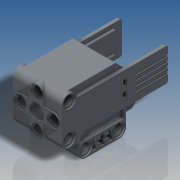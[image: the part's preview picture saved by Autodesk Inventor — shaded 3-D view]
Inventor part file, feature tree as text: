
AUTODESK INVENTOR PART (.ipt)
format: ipt  version: 2016 SP2 (Build 200236200, 236)  size: 1,027,584 bytes
history: native  units: in
note: dims shown in document units (in); Inventor stores cm internally (conversion verified against a paired STEP export)
features: extrude x12, sketch x7, plane x2, mirror x2, revolve x1, fillet x1
ambient origin geometry x8: Origin, YZ Plane, XZ Plane, XY Plane, X Axis, Y Axis, Z Axis, Center Point
bodies: Solid1 (feature_tree)
feature tree (25):
  sketch  "Sketch2"  dims[d1=0.5669in d2=45.0deg]
  extrude  "Extrusion1"  TaperAngle=45.0deg  [1 undecoded]
  sketch  "Sketch3"  dims[d3=0.1732in d4=0.2835in]
  extrude  "Extrusion3"  Depth=0.2835in
  extrude  "Extrusion4"  Depth=0.189in
  extrude  "Extrusion5"  Depth=1.0866in
  extrude  "Extrusion6"  Depth=0.2677in
  sketch  "Sketch5"  dims[d7=0.6299in d8=1.0866in]
  extrude  "Extrusion7"  Depth=0.0472in
  extrude  "Extrusion13"  Depth=0.0472in
  extrude  "Extrusion8"  Depth=0.0472in
  plane  "Work Plane1"
  revolve  "Revolution1"  [1 undecoded]
  mirror  "Mirror1"
  mirror  "Mirror2"
  extrude  "Extrusion9"  Depth=0.2835in
  plane  "Work Plane2"
  sketch  "Sketch8"  dims[d13=0.8189in d14=0.0in d18=2.0315in d19=0.0472in d20=0.315in d21=0.2835in d22=45.0deg d23=0.2441in d24=0.189in d25=0.063in d26=0.4567in d27=0.1732in d28=0.2835in d29=0.0472in d30=0.0472in d31=0.0787in d32=0.1102in d33=0.063in d34=0.0945in d35=1.1654in d36=0.3701in d37=0.0472in d38=0.1732in d39=0.252in d40=0.063in d41=0.0in d42=0.0472in d43=0.0in d44=0.252in d45=0.0in d46=0.2441in d47=0.0315in d48=0.0in d49=0.2441in d50=0.0315in d51=0.0in d54=1.5748in d56=0.0945in d57=0.3937in d59=0.3937in d61=0.0157in d62=0.0in d63=0.315in d64=0.189in d65=0.2441in d66=0.0315in d67=90.0deg d68=0.7244in d69=0.0in d70=0.0157in d71=0.2835in d72=0.2835in d73=0.6299in d74=0.189in d75=0.2441in d76=0.7244in d77=0.0in d78=0.7244in d79=0.0in d80=0.0315in d81=0.0in d82=0.063in d83=0.0in d84=0.0039in d85=0.0157in d86=0.6063in d87=0.0472in]
  extrude  "Extrusion10"  TaperAngle=45.0deg  [1 undecoded]
  extrude  "Extrusion11"  Depth=0.0472in
  extrude  "Extrusion12"  Depth=0.189in
  fillet  "Fillet1"  Radius=0.063in
  sketch  "Sketch4"  dims[d5=0.2441in d6=0.189in]
  sketch  "Sketch6"  dims[d9=1.4016in d10=0.2677in]
  sketch  "Sketch7"  dims[d11=0.0472in d12=0.0472in]
note: 3 required parameter values undecoded (feature->parameter linkage not recoverable at this tier; creation-order binding heuristic only, values carry confidence <= 0.55)